# Revit family: Reece_Accessory_Mizu_Drift_Toilet Roll Holder_Loop
name_source: partatom
category: Plumbing Fixtures
revit_build: Autodesk Revit 2018 (Build: 20180329_1100(x64)
units: mm (PartAtom-declared; Revit-internal decimal feet)

## family parameters
Always vertical = Yes
Cut with Voids When Loaded = Yes
Part Type = Normal
Room Calculation Point = Yes
Round Connector Dimension = Use Diameter
Shared = Yes
Work Plane-Based = Yes

## types (1)
- Chrome
    Default Elevation = 1000 mm
    Description = Toilet Roll Holder
    Disclaimer = THIS FILE IS THE PROPERTY OF THE REECE GROUP. IT MAY NOT BE REPRODUCED, REVERSE-ENGINEERED OR MODIFIED. ANY REPUBLICATION, TRANSMISSION OR DISTRIBUTION FOR THE PURPOSE OF COMMERCIALLY EXPLOITING THE FILES IS PROHIBITED.
    Keynote = Product #9501099, Reece_Accessory_Mizu_Drift_Toilet Roll Holder_Loop - Chrome
    Manufacturer = Mizu
    Model = Drift
    Reece_Accessory_Projection = 65 mm  [stored 0.213255 ft]
    Reece_Backplate Radius = 20 mm
    Reece_Detail_Disclaimer = THIS FILE IS THE PROPERTY OF THE REECE GROUP. IT MAY NOT BE REPRODUCED, REVERSE-ENGINEERED OR MODIFIED. ANY REPUBLICATION, TRANSMISSION OR DISTRIBUTION FOR THE PURPOSE OF COMMERCIALLY EXPLOITING THE FILES IS PROHIBITED.
    Reece_Detail_Shape = Loop
    Reece_Material_Main = Reece_Brass_Chrome
    Reece_Overall_Height = 102 mm
    Reece_Overall_Length = 135 mm
    Reece_Product_Brand = Mizu
    Reece_Product_Description = Mizu Drift Loop Toilet Roll Holder Chrome
    Reece_Product_Mount = Wall Mounted
    Reece_Product_Number = 9501099
    Reece_Product_Sub Brand = Drift
    Reece_Product_Type = Accessory
    Reece_Product_Web Page = https://www.reece.com.au
    Type Comments = Accessory
    URL = https://www.reece.com.au

note: [stored X ft] marks values corroborated as IEEE doubles in the binary element streams (Revit-internal decimal feet)

## geometry (parser evidence)
native form markers: Sweep x2
no freeform markers — native parametric forms only
